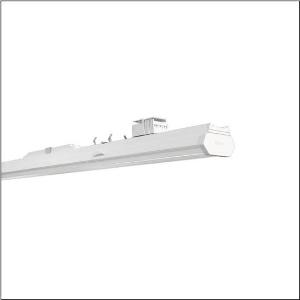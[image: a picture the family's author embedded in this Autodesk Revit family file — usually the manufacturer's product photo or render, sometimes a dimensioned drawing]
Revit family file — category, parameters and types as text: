
# Revit family: licross_r__21_protected_mo_52td12cn49xg_6de8
name_source: partatom
category: Lighting Fixtures
units: mm (PartAtom-declared; Revit-internal decimal feet)

## family parameters
Cut with Voids When Loaded = No
Host = Face
Light Source = No
Part Type = Normal
Room Calculation Point = No
Round Connector Dimension = Use Diameter
Shared = No

## types (1)
- --- (1 x LED, 9110 lm, 50.4 W, 4000K)
    Apparent Load = 50 VA
    CIE Flux Codes = 73 92 98 99 100
    Color Rendering = 80
    Color Temperature = 4000K
    Default Elevation = 1800 mm
    Description = Licross® 21 Protected MO, luminaire insert, of sheet steel, galvanised, coil coated, white, length: 1.500mm, width: 90mm, height: 103mm, LED rated luminous flux: 9.120lm, light colour: 840, control gear: ON/OFF Multilumen, CLOi, control gear: ECG Multilumen, with plug, 3-pole, with phase selection, mains connection: 220..240V, AC, 50/60Hz, start of lifetime: 50W, end of service life: 61W, halogen-free wiring, primary light control with lens, of plastic, primary optical cover: cover, of PMMA, light emission: direct distribution, primary light characteristic: symmetric, protection rating (complete): IP54, insulation class (complete): insulation class I (protective earthing), certification: CE, ENEC, VDE, UKCA, protection symbol: D if used in an environment with non-conductive dust loads with corresponding accessories, impact resistance: IK06, permissible ambient temperature for indoor applications: -35..+45°C, corresponds to IFS (International Featured Standards) requirements for safety and quality in the food industry, reducing of maximum allowable ambient temperature of 5°C with ceiling mounting, LABS conformity tested according to VDMA 24364:2018-05, packaging unit: 1 piece
    Height = 92 mm
    Lamp = 1 x LED
    Lamp Light Flux = 9110 lm
    Lamp Power = 50.4 W
    Lamp count = 1
    Length = 1500 mm
    Luminous efficacy = 181 lm/W
    Manufacturer = Siteco
    ModVariant = No
    Model = 52TD12CN49XG
    Mounting Place = Ceiling
    Mounting Type = Pendant
    Number of Poles = 1
    OnlyDefault = Yes
    Power Factor = 1
    Product Name = Licross® 21 Protected MO
    Product group = luminaire insert
    ProductGroupID = 901
    Protection Class = Protection class I
    Protection Degree = IP 54
    RLX_Detail_Level = 1
    RLX_Emergency_Light_Flux = 0 lm
    RLX_Emergency_Type = 0
    RLX_Emergency_Type_DB = No
    RlxData = <blob elided: 22193 chars, md5=0a67498c>
    Socket = socket
    Standby Power = 0 W
    System Light Flux = 9110 lm
    System Power = 50 W
    Type Comments = factory setting: luminous flux: 100 % | (A | C | E) | 117 mA
    Type Image = l_1256148.jpg
    URL = http://relux.com
    VarID = @adj_059447
    Voltage = 0 V
    Weight = 0.00 kg
    Width = 88 mm

## geometry (parser evidence)
native form markers: Blend x4, Sweep x11
no freeform markers — native parametric forms only
